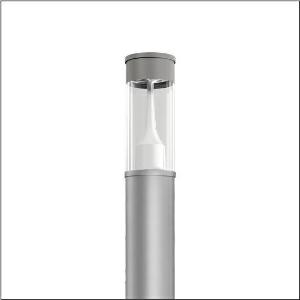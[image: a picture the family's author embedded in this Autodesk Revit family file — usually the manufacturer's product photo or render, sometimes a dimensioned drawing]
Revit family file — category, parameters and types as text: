
# Revit family: city-light_260_iq___pl1_2s_5xa5295cf14h_efd3
name_source: partatom
category: Lighting Fixtures
units: mm (PartAtom-declared; Revit-internal decimal feet)

## family parameters
Cut with Voids When Loaded = No
Host = Face
Light Source = No
Part Type = Normal
Room Calculation Point = No
Round Connector Dimension = Use Diameter
Shared = No

## types (1)
- --- (1 x LED, 2970 lm, 23.9 W, 2200K)
    Apparent Load = 24 VA
    CIE Flux Codes = 23 62 94 96 100
    Color Rendering = 70
    Color Temperature = 2200K
    Default Elevation = 1800 mm
    Description = City-Light 260 iQ, light pillar, Module 540 iQ-SR, primary light control with 3 zone facetted reflector, of plastic, silver coated, highly specular, structured, primary optical cover: cover, of PMMA, transparent, partly coated, light distribution: PL1.2s, primary light characteristic: symmetric, LED, High Power LED, rated luminous flux: 2.970lm, luminous efficacy: 124lm/W, light colour: 722, colour temperature: 2200K, control gear: ECG iQ, control: pre-setting: logarithmic dimming characteristic, Street-Remote, Auto-Match, Temp-Guard, Lumen-Switch, Night-Set, Smart-Wire, Light-Fading, Desk-Remote (wireless, voltage-free reading and setting of iQ features in the workshop via application-optimized NFC function/RFID function), optimised constant luminous flux control (CLO 2.0), with terminal, 6-pole, max. 2.5mm², mains connection: 230..240V, AC, 50/60Hz, start of lifetime: 24W, end of service life: 26W, reduction: 12W, luminaire housing, cylindrical, of extruded aluminium section, coated, Siteco® metallic grey (DB 702S), length: 2.600mm, diameter: 200mm, Module 540 iQ-SR, traffic white (RAL 9016), equipment: standard, protection rating (complete): IP65, insulation class (complete): insulation class II (safety insulation), certification: CE, ENEC, VDE, packaging unit: 1 piece

Light Distribution: PL1.2s
    Height = 500 mm
    Lamp = 1 x LED
    Lamp Light Flux = 2970 lm
    Lamp Power = 23.9 W
    Lamp count = 1
    Length = 200 mm  [stored 0.656168 ft]
    Luminous efficacy = 124 lm/W
    Manufacturer = Siteco
    ModVariant = No
    Model = 5XA5295CF14H
    Mounting Place = Floor
    Mounting Type = Freestanding
    Number of Poles = 1
    OnlyDefault = Yes
    Power Factor = 1
    Product Name = City-Light 260 iQ | PL1.2s
    Product group = light pillar
    ProductGroupID = 1301
    Protection Class = Protection class II
    Protection Degree = IP 65
    RLX_Detail_Level = 1
    RLX_Emergency_Light_Flux = 0 lm
    RLX_Emergency_Type = 0
    RLX_Emergency_Type_DB = No
    RlxData = <blob elided: 28821 chars, md5=7fce7c49>
    Socket = socket
    Standby Power = 0 W
    System Light Flux = 2970 lm
    System Power = 24 W
    Type Comments = factory setting: luminous flux: 100 % | dim-lin: 254 | 499 mA
    Type Image = l_1006920.jpg
    URL = http://relux.com
    VarID = @adj_115013
    Voltage = 0 V
    Weight = 0.00 kg
    Width = 0 mm  [stored 0 ft]

note: [stored X ft] marks values corroborated as IEEE doubles in the binary element streams (Revit-internal decimal feet)

## geometry (parser evidence)
native form markers: Blend x4, Sweep x9
no freeform markers — native parametric forms only
